# Revit family: ПСК-25
name_source: partatom
category: Арматура трубопроводов
units: mm (PartAtom-declared; Revit-internal decimal feet)

## family parameters
Всегда вертикально = Да
На основе рабочей плоскости = Нет
Общий = Нет
При загрузке вырезать с полостями = Нет
Размер круглого соединителя = Использовать диаметр
Тип детали = Клапан - Вставляется

## types (6) — shared parameters
ADSK_Единица измерения = шт.
ADSK_Завод-изготовитель = РУП "БЕЛГАЗТЕХНИКА"
ADSK_Класс герметичности по ГОСТ 9544-2005 = А
ADSK_Количество = 1
ADSK_Коэффициент расхода, а = 0,3
ADSK_Марка = ПСК-25
ADSK_Масса_Текст = 2,5 кг
ADSK_Тип соединения = муфтовое, резьба G1
zero-valued in all types: Отметка по умолчанию

## per-type parameters (varying)
| type | ADSK_Диапазон контролируемого давления, МПа | ADSK_Наименование |
| исполнение 00 | 0,0016-0,003 | Клапан предохранительный сбросной DN 25 ПСК-25-00 ТУ BY 100270876.155-2010 |
| исполнение 01 | 0,003-0,007 | Клапан предохранительный сбросной DN 25 ПСК-25-01 ТУ BY 100270876.155-2010 |
| исполнение 02 | 0,007-0,02 | Клапан предохранительный сбросной DN 25 ПСК-25-02 ТУ BY 100270876.155-2010 |
| исполнение 03 | 0,02-0,05 | Клапан предохранительный сбросной DN 25 ПСК-25-03 ТУ BY 100270876.155-2010 |
| исполнение 04 | 0,05-0,15 | Клапан предохранительный сбросной DN 25 ПСК-25-04 ТУ BY 100270876.155-2010 |
| исполнение 05 | 0,15-0,6 | Клапан предохранительный сбросной DN 25 ПСК-25-05 ТУ BY 100270876.155-2010 |
